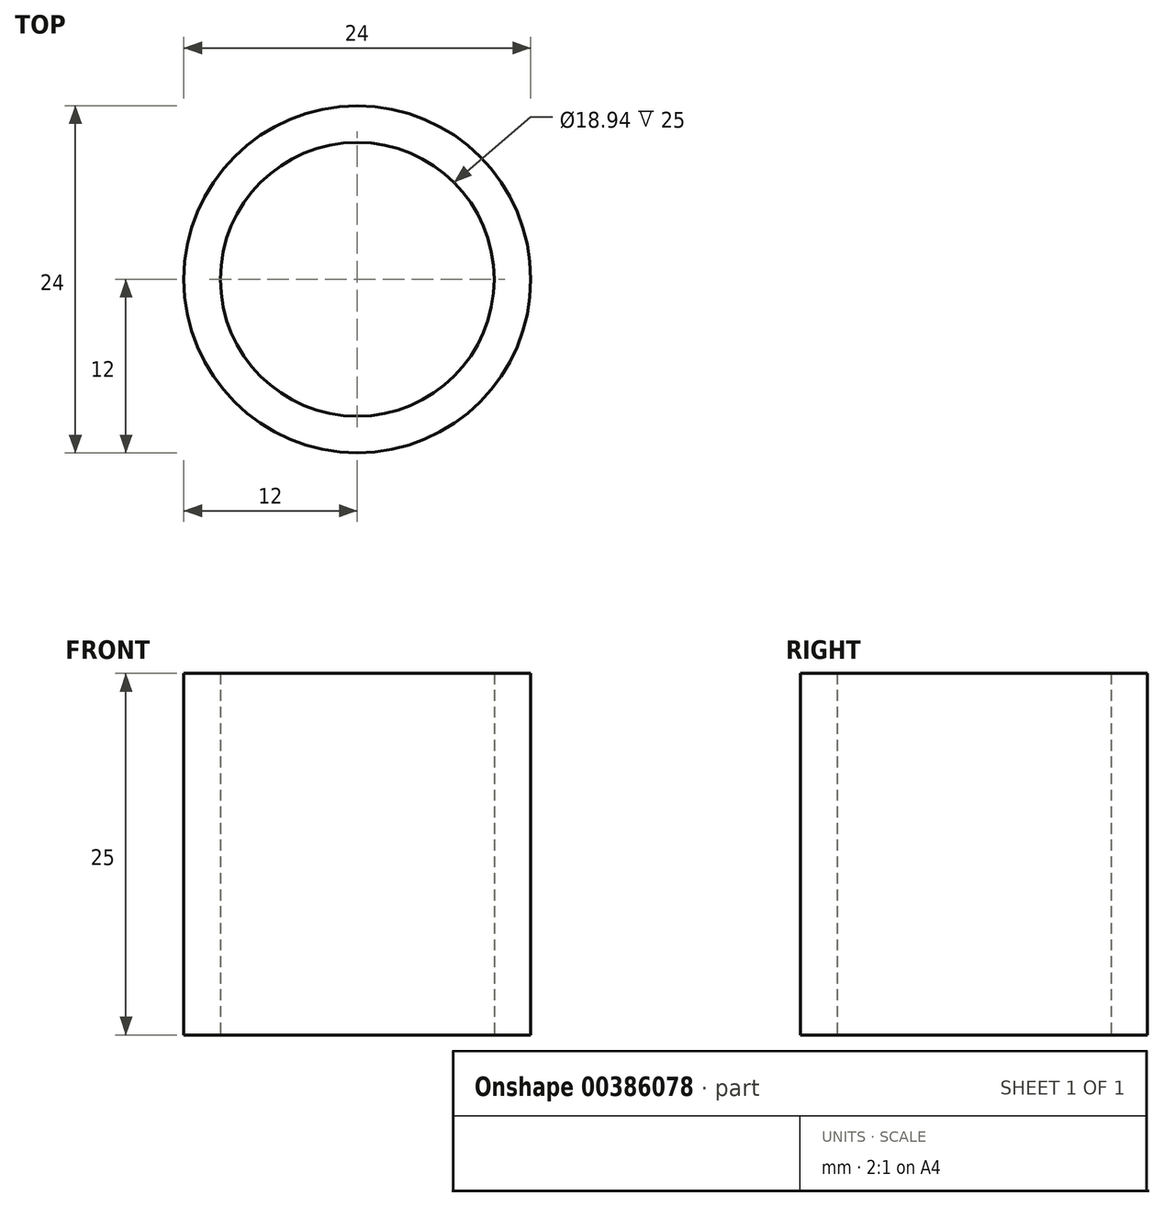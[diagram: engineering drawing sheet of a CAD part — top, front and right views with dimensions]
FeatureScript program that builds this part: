
annotation { "Feature Type Name" : "Feature", "Feature Type Description" : "" }
export const myFeature = defineFeature(function(context is Context, id is Id, definition is map)
    precondition{}
    {
        {
            var Q0;
            Q0=qCreatedBy(makeId("Top.planeOp"),FACE);
            var sketch = newSketch(context, id + "F0", { "sketchPlane" : qUnion([Q0])});
            skCircle(sketch, "E0", {"center": v(0, 0) * mm, "radius": 12 * mm});
            skCircle(sketch, "E1", {"center": v(0, 0) * mm, "radius": 9.47 * mm});
            skCircle(sketch, "E2", {"center": v(0, 0) * mm, "radius": 7.5 * mm});
            skSolve(sketch);
        }
        {
            var Q0;
            Q0=makeQuery(id+"F0.imprint","IMPRINT",FACE,{"disambiguationData":[TD([[makeQuery(id+"F0.imprint","IMPRINT",EDGE,{"derivedFrom":sQuery(id+"F0.wireOp",EDGE,"E0")}),1.0]])]});
            extrude(context, id + "F1", {"entities" : qUnion([Q0]), "depth" : 25 * mm});
        }
    });
